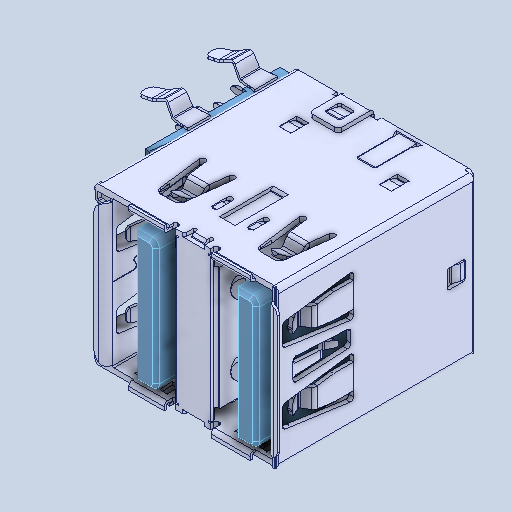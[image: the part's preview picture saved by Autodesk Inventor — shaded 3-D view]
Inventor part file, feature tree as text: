
AUTODESK INVENTOR PART (.ipt)
format: ipt  version: 2022 (Build 260153000, 153)  size: 2,134,016 bytes
history: mixed  units: in
note: dims shown in document units (in); Inventor stores cm internally (conversion verified against a paired STEP export)
features: chamfer x26, other x24, mirror x15, fillet x6, imported_body x1
ambient origin geometry x8: Origin, YZ Plane, XZ Plane, XY Plane, X Axis, Y Axis, Z Axis, Center Point
bodies: Solid1 (imported_parasolid), Solid2 (imported_parasolid), Solid3 (imported_parasolid), Solid4 (imported_parasolid), Solid5 (imported_parasolid), Solid6 (imported_parasolid), Solid7 (imported_parasolid), Solid8 (imported_parasolid), Solid9 (imported_parasolid), Solid10 (imported_parasolid), Solid11 (imported_parasolid), Solid12 (imported_parasolid), Solid13 (imported_parasolid), Solid14 (imported_parasolid), Solid15 (imported_parasolid), Solid16 (imported_parasolid), Solid17 (imported_parasolid), Solid18 (imported_parasolid), Solid19 (imported_parasolid), Solid20 (imported_parasolid), Solid21 (imported_parasolid), Solid22 (imported_parasolid), Solid23 (imported_parasolid), Solid24 (imported_parasolid), Solid25 (imported_parasolid), Solid26 (imported_parasolid), Solid27 (imported_parasolid), Solid28 (imported_parasolid), Solid29 (imported_parasolid), Solid30 (imported_parasolid), Solid31 (imported_parasolid), Solid32 (imported_parasolid), Solid33 (imported_parasolid), Solid34 (imported_parasolid), Solid35 (imported_parasolid), Solid36 (imported_parasolid), Solid37 (imported_parasolid), Solid38 (imported_parasolid), Solid39 (imported_parasolid), Solid40 (imported_parasolid), Solid41 (imported_parasolid), Solid42 (imported_parasolid), Solid43 (imported_parasolid), Solid44 (imported_parasolid), Solid45 (imported_parasolid), Solid46 (imported_parasolid), Solid47 (imported_parasolid), Solid48 (imported_parasolid), Solid49 (imported_parasolid), Solid50 (imported_parasolid), Solid51 (imported_parasolid), Solid52 (imported_parasolid), Solid53 (imported_parasolid), Solid54 (imported_parasolid), Solid55 (imported_parasolid), Solid56 (imported_parasolid), Solid57 (imported_parasolid), Solid58 (imported_parasolid), Solid59 (imported_parasolid), Solid60 (imported_parasolid), Solid61 (imported_parasolid), Solid62 (imported_parasolid), Solid63 (imported_parasolid), Solid64 (imported_parasolid), Solid65 (imported_parasolid), Solid66 (imported_parasolid), Solid67 (imported_parasolid), Solid68 (imported_parasolid), Solid69 (imported_parasolid), Solid70 (imported_parasolid), Solid71 (imported_parasolid)
feature tree (72):
  other  "Cut-Extrude5[1]"
  other  "Cut-Extrude5[2]"
  other  "Cut-Extrude5[3]"
  other  "Cut-Extrude11[3]"
  other  "Cut-Extrude11[4]"
  other  "Cut-Extrude13[1]"
  other  "Cut-Extrude13[2]"
  mirror  "Mirror8[1]"
  mirror  "Mirror8[2]"
  chamfer  "Chamfer4"  [1 undecoded]
  chamfer  "Chamfer5"  [1 undecoded]
  other  "Boss-Extrude14"
  other  "LPattern1"
  mirror  "Mirror9[1]"
  mirror  "Mirror9[2]"
  other  "LPattern2[1]"
  other  "LPattern2[2]"
  other  "LPattern2[3]"
  other  "LPattern2[4]"
  fillet  "Fillet4"  [1 undecoded]
  fillet  "Fillet5"  [1 undecoded]
  fillet  "Fillet6"  [1 undecoded]
  fillet  "Fillet7"  [1 undecoded]
  other  "Cut-Extrude22"
  other  "Cut-Extrude23[1]"
  other  "Cut-Extrude23[2]"
  other  "Cut-Extrude23[3]"
  mirror  "Mirror18"
  chamfer  "Chamfer8"  [1 undecoded]
  chamfer  "Chamfer9"  [1 undecoded]
  chamfer  "Chamfer10"  [1 undecoded]
  fillet  "Fillet9"  [1 undecoded]
  other  "Cut-Extrude28"
  other  "Body-Move_Copy1[1]"
  other  "Body-Move_Copy1[2]"
  mirror  "Mirror19[1]"
  mirror  "Mirror19[2]"
  mirror  "Mirror19[3]"
  mirror  "Mirror19[4]"
  other  "Cut-Extrude31[1]"
  other  "Cut-Extrude31[2]"
  mirror  "Mirror23[1]"
  mirror  "Mirror23[2]"
  chamfer  "Chamfer14"  [1 undecoded]
  chamfer  "Chamfer15"  [1 undecoded]
  other  "Cut-Extrude34[1]"
  other  "Cut-Extrude34[2]"
  mirror  "Mirror27[1]"
  mirror  "Mirror27[2]"
  mirror  "Mirror29[1]"
  mirror  "Mirror29[2]"
  fillet  "Fillet13"  [1 undecoded]
  chamfer  "Chamfer19"  [1 undecoded]
  chamfer  "Chamfer20"  [1 undecoded]
  chamfer  "Chamfer21"  [1 undecoded]
  chamfer  "Chamfer22"  [1 undecoded]
  chamfer  "Chamfer23"  [1 undecoded]
  chamfer  "Chamfer24"  [1 undecoded]
  chamfer  "Chamfer25"  [1 undecoded]
  chamfer  "Chamfer26"  [1 undecoded]
  chamfer  "Chamfer27"  [1 undecoded]
  chamfer  "Chamfer28"  [1 undecoded]
  chamfer  "Chamfer29"  [1 undecoded]
  chamfer  "Chamfer30"  [1 undecoded]
  chamfer  "Chamfer31"  [1 undecoded]
  chamfer  "Chamfer32"  [1 undecoded]
  chamfer  "Chamfer33"  [1 undecoded]
  chamfer  "Chamfer34"  [1 undecoded]
  chamfer  "Chamfer35"  [1 undecoded]
  chamfer  "Chamfer36"  [1 undecoded]
  chamfer  "Chamfer38"  [1 undecoded]
  imported_body  NMx_Import_Brep_tag  [imported B-rep: ~72 faces, bbox_mm=None]
note: 32 required parameter values undecoded (feature->parameter linkage not recoverable at this tier; creation-order binding heuristic only, values carry confidence <= 0.55)
